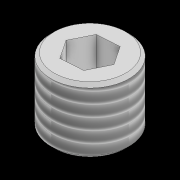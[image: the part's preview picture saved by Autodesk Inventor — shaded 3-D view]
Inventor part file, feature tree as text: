
AUTODESK INVENTOR PART (.ipt)
format: ipt  version: 2021 (Build 250183000, 183)  size: 112,640 bytes
history: native  units: mm
features: extrude x2, sketch x2, thread x1, chamfer x1
ambient origin geometry x8: Origin, YZ Plane, XZ Plane, XY Plane, X Axis, Y Axis, Z Axis, Center Point
bodies: Solid1 (feature_tree)
feature tree (6):
  extrude  "Extrusion1"  Depth=6.0mm
  extrude  "Extrusion2"  Depth=5.5mm TaperAngle=0.0deg
  thread  "Thread1"  [1 undecoded]
  chamfer  "Chamfer1"  Distance=0.5mm Angle=45.0deg
  sketch  "Sketch1"  dims[d0=10.0mm d1=0.0mm d2=6.0mm]
  sketch  "Sketch2"  dims[d3=12.0mm d4=5.5mm d5=0.0mm d6=10.0mm d7=0.0mm d8=0.5mm d9=2.0mm d10=45.0deg]
note: 1 required parameter value undecoded (feature->parameter linkage not recoverable at this tier; creation-order binding heuristic only, values carry confidence <= 0.55)
